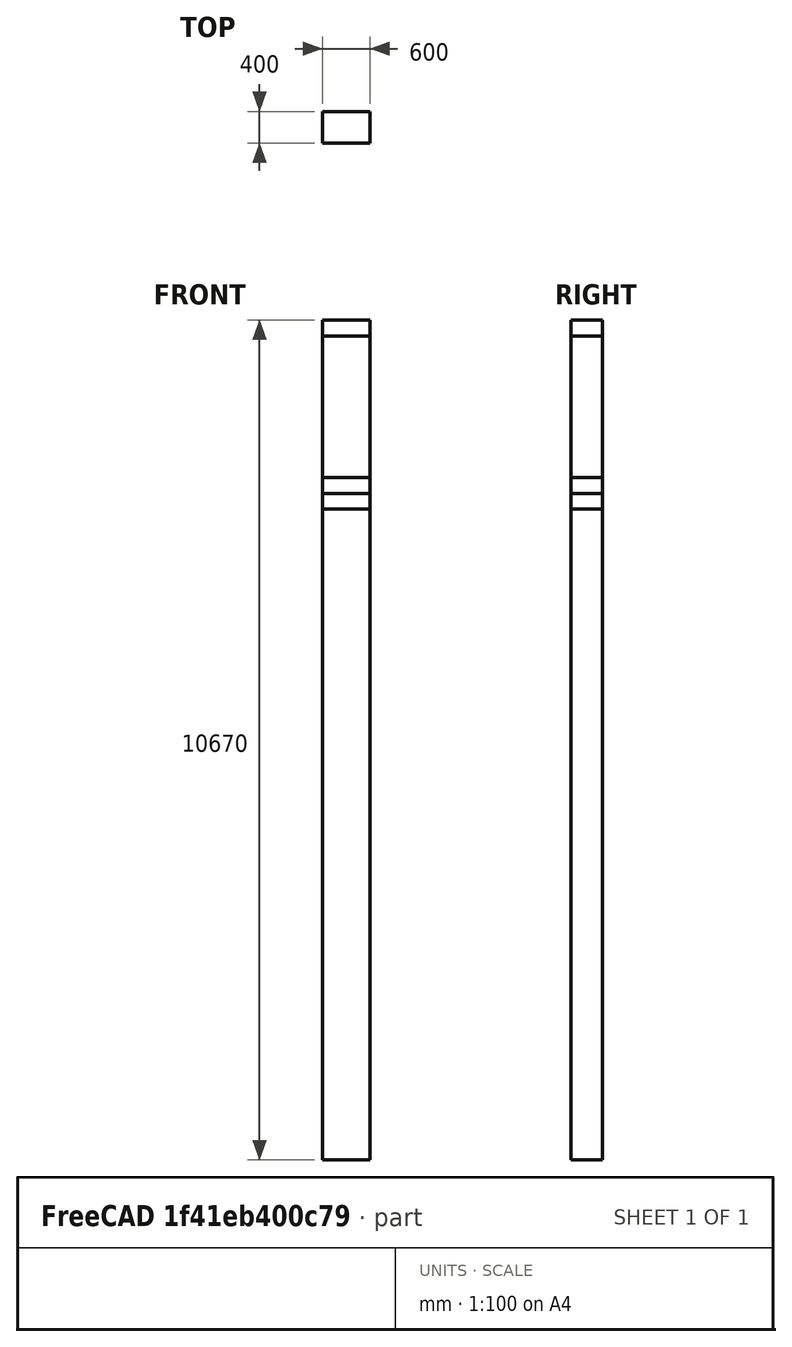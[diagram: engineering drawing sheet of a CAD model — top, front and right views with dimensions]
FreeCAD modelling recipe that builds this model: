
FCSTD DOCUMENT  (FreeCAD 0.21R33694 (Git))
Label: column_3_with_mast
License: All rights reserved
LicenseURL: http://en.wikipedia.org/wiki/All_rights_reserved
objects: Fem::ConstraintForce×10, Part::FeaturePython×7, Part::Feature×5, Part::Plane×4, Fem::ConstraintFixed×2, Fem::FemSolverObjectPython×1, App::MaterialObjectPython×1, Part::Box×1, Fem::FemMeshObjectPython×1, Fem::FemAnalysis×1
note: 17 computed .brp shape members not serialized (recipe doc carries the construction recipe); baked Part::Feature solids carry a one-line shape summary decoded from their .brp

FEATURE [Fem::FemSolverObjectPython] SolverCcxTools  # FEM object (typed FeaturePython)
  AnalysisType = 0
  BeamShellResultOutput3D = true
  BucklingFactors = 1
  EigenmodeHighLimit = 1000000
  EigenmodeLowLimit = 0
  EigenmodesCount = 10
  GeometricalNonlinearity = 0
  IterationsControlParameterCutb = 0.25,0.5,0.75,0.85,,,1.5,
  IterationsControlParameterIter = 4,8,9,200,10,400,,200,,
  IterationsControlParameterTimeUse = false
  IterationsThermoMechMaximum = 2000
  IterationsUserDefinedIncrementations = false
  IterationsUserDefinedTimeStepLength = false
  MaterialNonlinearity = 0
  MatrixSolverType = 0
  SplitInputWriter = true
  ThermoMechSteadyState = true
  TimeEnd = 1
  TimeInitialStep = 0.01
FEATURE [App::MaterialObjectPython] MaterialSolid  label="B450"  # material (typed FeaturePython)
  Category = 0
  Material = AngleOfFriction=30 deg,AuthorAndLicense=(c) 2019 Bernd Hahnebach (CC-BY 3.0),CardName=Concrete-EN-C35_45,CompressiveStrength=15.75 MPa,+7 more (map truncated)
FEATURE [Fem::ConstraintFixed] ConstraintFixed  label="support"
  NormalDirection = (0,0,-1)
FEATURE [Part::Box] Box  label="Cube"
  AttacherType = Attacher::AttachEngine3D
  Height = 10670
  Length = 600
  Width = 400
FEATURE [Part::Plane] Plane
  AttacherType = Attacher::AttachEngine3D
  Length = 600
  Placement = pos=(0,0,8270) rot=(0,0,1;0rad)
  Width = 400
FEATURE [Part::Plane] Plane002
  AttacherType = Attacher::AttachEngine3D
  Length = 600
  Placement = pos=(0,0,8470) rot=(0,0,1;0rad)
  Width = 400
FEATURE [Part::Plane] Plane003
  AttacherType = Attacher::AttachEngine3D
  Length = 600
  Placement = pos=(0,0,8670) rot=(0,0,1;0rad)
  Width = 400
FEATURE [Part::Plane] Plane004
  AttacherType = Attacher::AttachEngine3D
  Length = 600
  Placement = pos=(0,0,10470) rot=(0,0,1;0rad)
  Width = 400
FEATURE [Part::FeaturePython] Slice  # WARN: FeaturePython — macro-defined, semantics opaque (R4)
  Base = -> Box
  Mode = 1
  Tolerance = 0
  Tools = -> [Plane,Plane002,Plane003,Plane004]
FEATURE [Part::FeaturePython] Slice_child0  label="Slice.0"  # WARN: FeaturePython — macro-defined, semantics opaque (R4)
  Base = -> Slice
  FilterType = 1
  Invert = false
  OverrideMaxVal = 0
  WindowFrom = 80
  WindowTo = 100
  items = 0
FEATURE [Part::FeaturePython] Slice_child1  label="Slice.1"  # WARN: FeaturePython — macro-defined, semantics opaque (R4)
  Base = -> Slice
  FilterType = 1
  Invert = false
  OverrideMaxVal = 0
  WindowFrom = 80
  WindowTo = 100
  items = 1
FEATURE [Fem::ConstraintForce] ConstraintForce004  label="crane_V2(p)"
  Direction = -> Slice_child1 [Edge3]
  DirectionVector = (0,0,1)
  Force = 250000
  NormalDirection = (-1,0,0)
  Points = (16) [(0,400,8270),(0,400,8336.67),(0,400,8403.33),(0,400,8470),(0,266.667,8270),(0,266.667,8336.67),(0,266.667,8403.33),(0,266.667,8470),(0,133.333,8270),+7 more]
  References = -> [Slice_child1]
  Scale = 19
FEATURE [Part::FeaturePython] Slice_child2  label="Slice.2"  # WARN: FeaturePython — macro-defined, semantics opaque (R4)
  Base = -> Slice
  FilterType = 1
  Invert = false
  OverrideMaxVal = 0
  WindowFrom = 80
  WindowTo = 100
  items = 2
FEATURE [Fem::ConstraintForce] ConstraintForce003  label="crane_V1(p)"
  Direction = -> Slice_child2 [Edge5]
  DirectionVector = (0,0,-1)
  Force = 550000
  NormalDirection = (1,0,0)
  Points = (16) [(600,400,8270),(600,400,8336.67),(600,400,8403.33),(600,400,8470),(600,266.667,8270),(600,266.667,8336.67),(600,266.667,8403.33),(600,266.667,8470),+8 more]
  References = -> [Slice_child1]
  Reversed = true
  Scale = 19
FEATURE [Fem::ConstraintForce] ConstraintForce005  label="mast_F_bottom"
  DirectionVector = (-1,0,0)
  Force = 9430
  NormalDirection = (-1,0,0)
  Points = (16) [(0,400,8470),(0,400,8536.67),(0,400,8603.33),(0,400,8670),(0,266.667,8470),(0,266.667,8536.67),(0,266.667,8603.33),(0,266.667,8670),(0,133.333,8470),+7 more]
  References = -> [Slice_child2]
  Scale = 19
FEATURE [Part::FeaturePython] Slice_child3  label="Slice.3"  # WARN: FeaturePython — macro-defined, semantics opaque (R4)
  Base = -> Slice
  FilterType = 1
  Invert = false
  OverrideMaxVal = 0
  WindowFrom = 80
  WindowTo = 100
  items = 3
FEATURE [Part::FeaturePython] Slice_child4  label="Slice.4"  # WARN: FeaturePython — macro-defined, semantics opaque (R4)
  Base = -> Slice
  FilterType = 1
  Invert = false
  OverrideMaxVal = 0
  WindowFrom = 80
  WindowTo = 100
  items = 4
FEATURE [Fem::ConstraintForce] ConstraintForce  label="wind"
  DirectionVector = (1,0,0)
  Force = 41600
  NormalDirection = (-1,0,0)
  Points = (132) [(0,400,10470),(0,400,10536.7),(0,400,10603.3),(0,400,10670),(0,266.667,10470),(0,266.667,10536.7),(0,266.667,10603.3),(0,266.667,10670),+124 more]
  References = -> [Slice_child4,Slice_child3,Slice_child2,Slice_child1,Slice_child0]
  Reversed = true
  Scale = 59
FEATURE [Fem::ConstraintForce] ConstraintForce001  label="mast_F_top"
  DirectionVector = (1,0,0)
  Force = 12820
  NormalDirection = (-1,0,0)
  Points = (16) [(0,400,10470),(0,400,10536.7),(0,400,10603.3),(0,400,10670),(0,266.667,10470),(0,266.667,10536.7),(0,266.667,10603.3),(0,266.667,10670),+8 more]
  References = -> [Slice_child4]
  Reversed = true
  Scale = 19
FEATURE [Fem::ConstraintForce] ConstraintForce002  label="roof_girder_R(p)"
  DirectionVector = (0,0,-1)
  Force = 100000
  NormalDirection = (0,0,1)
  Points = (16) [(0,0,10670),(200,0,10670),(400,0,10670),(600,0,10670),(0,133.333,10670),(200,133.333,10670),(400,133.333,10670),(600,133.333,10670),(0,266.667,10670),+7 more]
  References = -> [Slice_child4]
  Reversed = true
  Scale = 24
FEATURE [Part::Feature] Solid
  shape: bbox 600 x 400 x 8270 mm, 6 faces (baked)
FEATURE [Part::Feature] Solid001
  shape: bbox 600 x 400 x 200 mm, 6 faces (baked)
FEATURE [Part::Feature] Solid002
  shape: bbox 600 x 400 x 200 mm, 6 faces (baked)
FEATURE [Part::Feature] Solid003
  shape: bbox 600 x 400 x 1800 mm, 6 faces (baked)
FEATURE [Part::Feature] Solid004
  shape: bbox 600 x 400 x 200 mm, 6 faces (baked)
FEATURE [Part::FeaturePython] BooleanFragments  # WARN: FeaturePython — macro-defined, semantics opaque (R4)
  Mode = 2
  Objects = -> [Solid,Solid001,Solid002,Solid003,Solid004]
  Tolerance = 0
FEATURE [Fem::FemMeshObjectPython] FEMMeshGmsh  # FEM object (typed FeaturePython)
  Algorithm2D = 0
  Algorithm3D = 0
  CharacteristicLengthMax = 400
  CharacteristicLengthMin = 0
  CoherenceMesh = true
  ElementDimension = 0
  ElementOrder = 1
  GeometryTolerance = 1e-06
  GroupsOfNodes = false
  HighOrderOptimize = 0
  MeshSizeFromCurvature = 12
  OptimizeNetgen = false
  OptimizeStd = true
  Part = -> BooleanFragments
  RecombinationAlgorithm = 0
  Recombine3DAll = false
  RecombineAll = false
  SecondOrderLinear = false
FEATURE [Fem::ConstraintFixed] ConstraintFixed001  label="foundation"
  NormalDirection = (0,0,-1)
  Normals = (16) [(0,0,-1),(0,0,-1),(0,0,-1),(0,0,-1),(0,0,-1),(0,0,-1),(0,0,-1),(0,0,-1),(0,0,-1),(0,0,-1),(0,0,-1),(0,0,-1),(0,0,-1),(0,0,-1),(0,0,-1),(0,0,-1)]
  Points = (16) [(0,0,0),(200,0,0),(400,0,0),(600,0,0),(0,133.333,0),(200,133.333,0),(400,133.333,0),(600,133.333,0),(0,266.667,0),(200,266.667,0),(400,266.667,0),+5 more]
  References = -> [Slice_child0]
  Scale = 24
FEATURE [Fem::ConstraintForce] ConstraintForce006  label="mast_H1_top"
  Direction = -> Slice_child4 [Edge2]
  DirectionVector = (0,1,0)
  Force = 17100
  NormalDirection = (-1,0,0)
  Points = (16) [(0,400,10470),(0,400,10536.7),(0,400,10603.3),(0,400,10670),(0,266.667,10470),(0,266.667,10536.7),(0,266.667,10603.3),(0,266.667,10670),+8 more]
  References = -> [Slice_child4]
  Scale = 19
FEATURE [Fem::ConstraintForce] ConstraintForce007  label="mast_H2_top"
  Direction = -> Slice_child4 [Edge9]
  DirectionVector = (0,-1,0)
  Force = 4270
  NormalDirection = (1,0,0)
  Points = (16) [(600,400,10470),(600,400,10536.7),(600,400,10603.3),(600,400,10670),(600,266.667,10470),(600,266.667,10536.7),(600,266.667,10603.3),+9 more]
  References = -> [BooleanFragments]
  Reversed = true
  Scale = 19
FEATURE [Fem::ConstraintForce] ConstraintForce008  label="mast_H1_bottom"
  Direction = -> Slice_child2 [Edge2]
  DirectionVector = (0,-1,0)
  Force = 12570
  NormalDirection = (-1,0,0)
  Points = (16) [(0,400,8470),(0,400,8536.67),(0,400,8603.33),(0,400,8670),(0,266.667,8470),(0,266.667,8536.67),(0,266.667,8603.33),(0,266.667,8670),(0,133.333,8470),+7 more]
  References = -> [Slice_child2]
  Reversed = true
  Scale = 19
FEATURE [Fem::ConstraintForce] ConstraintForce009  label="mast_H2_bottom"
  Direction = -> Slice_child2 [Edge8]
  DirectionVector = (0,1,0)
  Force = 3140
  NormalDirection = (1,0,0)
  Points = (16) [(600,400,8470),(600,400,8536.67),(600,400,8603.33),(600,400,8670),(600,266.667,8470),(600,266.667,8536.67),(600,266.667,8603.33),(600,266.667,8670),+8 more]
  References = -> [Slice_child2]
  Scale = 19
FEATURE [Fem::FemAnalysis] Analysis
  Group = -> [SolverCcxTools,MaterialSolid,ConstraintForce,ConstraintForce001,ConstraintForce002,ConstraintFixed,ConstraintForce003,ConstraintForce004,ConstraintForce005,FEMMeshGmsh,ConstraintFixed001,ConstraintForce006,ConstraintForce007,ConstraintForce008,ConstraintForce009]
